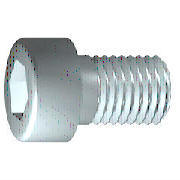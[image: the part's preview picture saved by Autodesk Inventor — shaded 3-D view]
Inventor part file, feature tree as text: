
AUTODESK INVENTOR PART (.ipt)
format: ipt  version: 2025 (Build 290162000, 162)  size: 194,560 bytes
history: native  units: mm (DEFAULTED — no unit token found)
features: extrude x1, plane x1, fillet x1
ambient origin geometry x7: Origin, YZ Plane, XY Plane, X Axis, Y Axis, Z Axis, Center Point
bodies: Solid1 (feature_tree), Body (feature_tree)
feature tree (3):
  extrude  "Slot"  Depth=18.1731mm
  plane  "Work Plane1"
  fillet  "Fillet2"  Radius=0.61355mm
